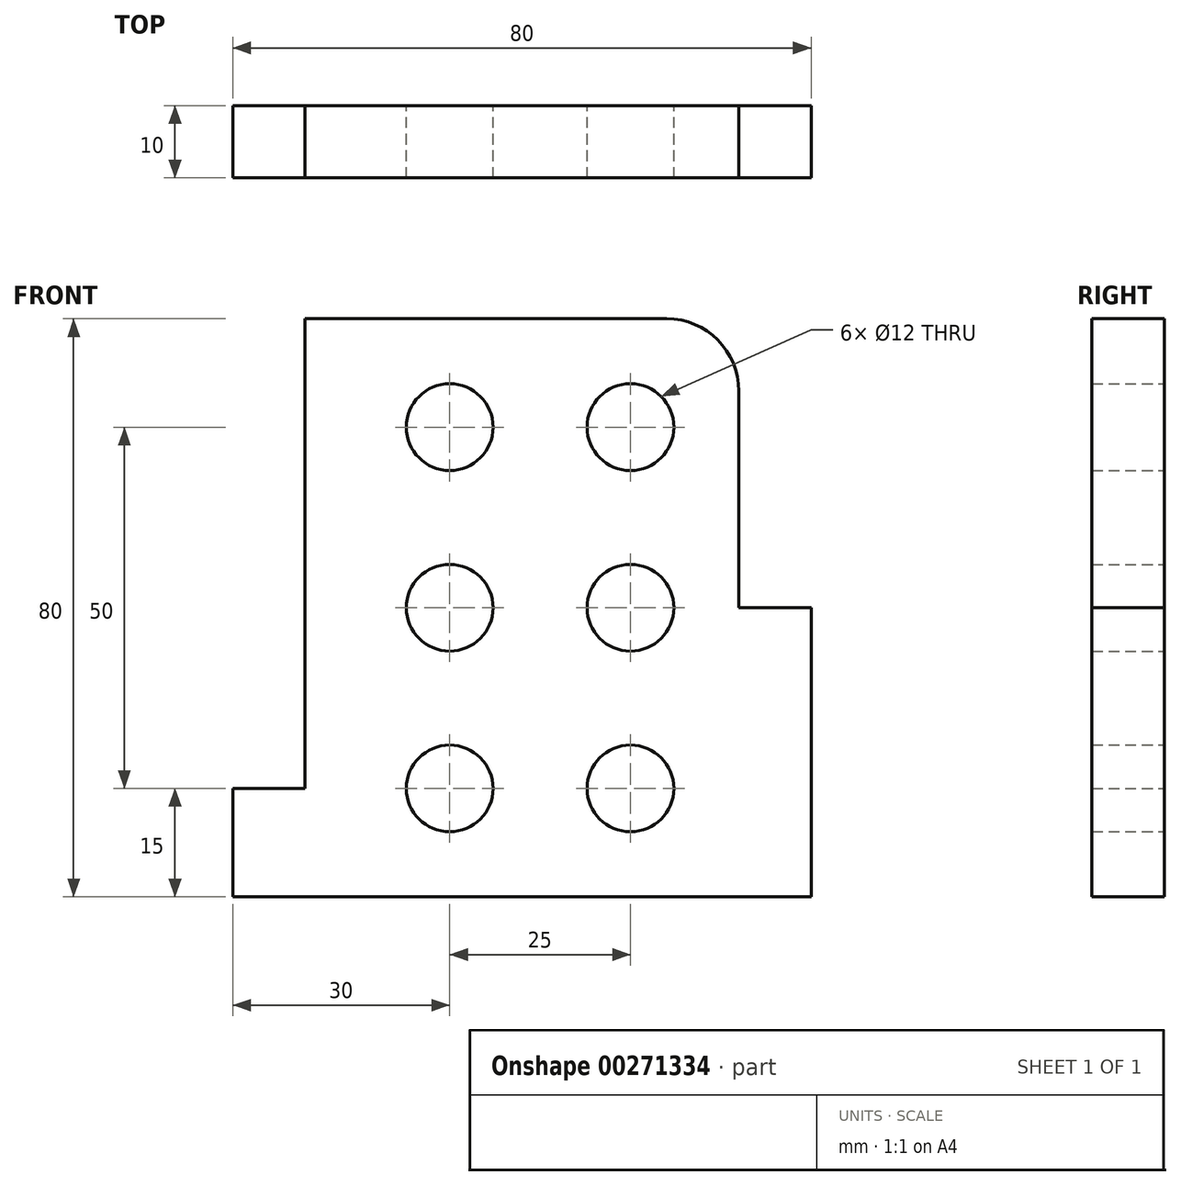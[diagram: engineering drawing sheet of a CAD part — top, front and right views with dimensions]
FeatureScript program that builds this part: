
annotation { "Feature Type Name" : "Feature", "Feature Type Description" : "" }
export const myFeature = defineFeature(function(context is Context, id is Id, definition is map)
    precondition{}
    {
        {
            var Q0;
            Q0=qCreatedBy(makeId("Front.planeOp"),FACE);
            var sketch = newSketch(context, id + "F0", { "sketchPlane" : qUnion([Q0])});
            skLineSegment(sketch, "E0", {"start": v(0, 0) * mm, "end": v(80, 0) * mm});
            skLineSegment(sketch, "E1", {"start": v(0, 0) * mm, "end": v(0, 15) * mm});
            skLineSegment(sketch, "E2", {"start": v(80, 0) * mm, "end": v(80, 40) * mm});
            skLineSegment(sketch, "E3", {"start": v(0, 15) * mm, "end": v(10, 15) * mm});
            skLineSegment(sketch, "E4", {"start": v(10, 15) * mm, "end": v(10, 80) * mm});
            skLineSegment(sketch, "E5", {"start": v(10, 15) * mm, "end": v(10, 65) * mm});
            skLineSegment(sketch, "E6", {"start": v(10, 80) * mm, "end": v(60, 80) * mm});
            skArc(sketch, "E7", {"start": v(70, 70) * mm, "mid": v(67.07, 77.07) * mm, "end": v(60, 80) * mm});
            skLineSegment(sketch, "E8", {"start": v(70, 70) * mm, "end": v(70, 40) * mm});
            skLineSegment(sketch, "E9", {"start": v(70, 40) * mm, "end": v(80, 40) * mm});
            skCircle(sketch, "E10", {"center": v(30, 65) * mm, "radius": 6 * mm});
            skCircle(sketch, "E11", {"center": v(55, 65) * mm, "radius": 6 * mm});
            skCircle(sketch, "E12", {"center": v(30, 40) * mm, "radius": 6 * mm});
            skCircle(sketch, "E13", {"center": v(55, 40) * mm, "radius": 6 * mm});
            skCircle(sketch, "E14", {"center": v(30, 15) * mm, "radius": 6 * mm});
            skCircle(sketch, "E15", {"center": v(55, 15) * mm, "radius": 6 * mm});
            skSolve(sketch);
        }
        {
            var Q0;
            Q0=makeQuery(id+"F0.imprint","IMPRINT",FACE,{"disambiguationData":[TD([[makeQuery(id+"F0.imprint","IMPRINT",EDGE,{"derivedFrom":sQuery(id+"F0.wireOp",EDGE,"E0")}),1.0]])]});
            extrude(context, id + "F1", {"entities" : qUnion([Q0]), "depth" : 10 * mm});
        }
    });
